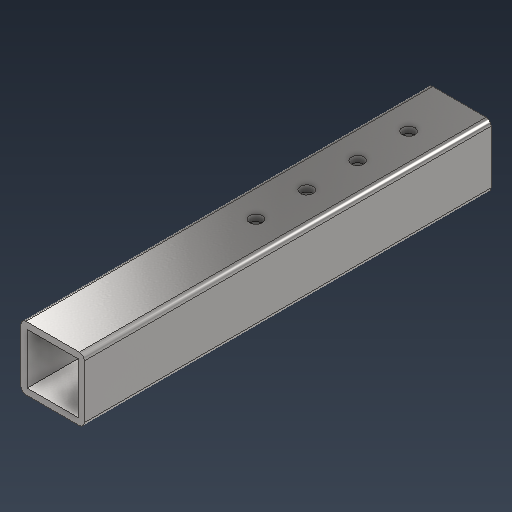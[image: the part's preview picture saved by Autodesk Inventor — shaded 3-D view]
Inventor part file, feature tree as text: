
AUTODESK INVENTOR PART (.ipt)
format: ipt  version: 2021 (Build 250183000, 183)  size: 222,208 bytes
history: native  units: mm
features: plane x2, split x2, sketch x2, extrude x1, fillet x1, hole x1, pattern_linear x1
ambient origin geometry x8: Origin, YZ Plane, XZ Plane, XY Plane, X Axis, Y Axis, Z Axis, Center Point
bodies: Solid1 (feature_tree), Solid2 (feature_tree), Solid3 (feature_tree)
feature tree (10):
  extrude  "Extrusion1"  Depth=25.0mm
  fillet  "Fillet1"  Radius=12.5mm
  plane  "Work Plane1"
  split  "Split1"
  hole  "Hole1"  [1 undecoded]
  pattern_linear  "Rectangular Pattern1"  Count1=100 Spacing1=0.0mm
  plane  "Work Plane3"
  split  "Split3"
  sketch  "Sketch1"  dims[d0=25.0mm d1=25.0mm d2=12.5mm]
  sketch  "Sketch2"  dims[d3=12.5mm d4=2.5mm d5=1000.0mm d6=0.0mm d7=2.0mm d8=-160.0mm d9=0.0mm d10=20.0mm d11=5.0mm d12=6.0mm d13=4.0mm d14=2.0mm d15=90.0deg d16=8.0mm d17=20.594885mm d18=40.0mm d20=20.0mm d22=-24.5mm]
note: 1 required parameter value undecoded (feature->parameter linkage not recoverable at this tier; creation-order binding heuristic only, values carry confidence <= 0.55)
